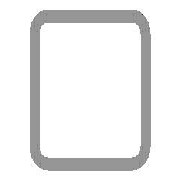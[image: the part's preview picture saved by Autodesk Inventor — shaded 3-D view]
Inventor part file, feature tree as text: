
AUTODESK INVENTOR PART (.ipt)
format: ipt  version: 2025 (Build 290162010, 162A)  size: 132,608 bytes
history: native  units: mm (DEFAULTED — no unit token found)
features: other x4, sketch x1, plane x1
ambient origin geometry x8: Origin, YZ Plane, XZ Plane, XY Plane, X Axis, Y Axis, Z Axis, Center Point
bodies: Solid1 (feature_tree), Body (feature_tree)
feature tree (6):
  parser-record x1  (decoder bookkeeping rows leaked as tree rows — omitted from the tree; the rows remain in map.json)
  other  "Driven Length"
  other  "Start Plane"
  other  "End Plane"
  sketch  "Sketch3"  dims[d3=700.0mm d4=0.0mm d7=6.0mm d9=80.0mm d11=80.0mm d12=3.0mm d13=-0.0mm d14=700.0mm d15=40.0mm d16=40.0mm d17=90.0deg d18=700.0mm]
  plane  "Work Plane3"
